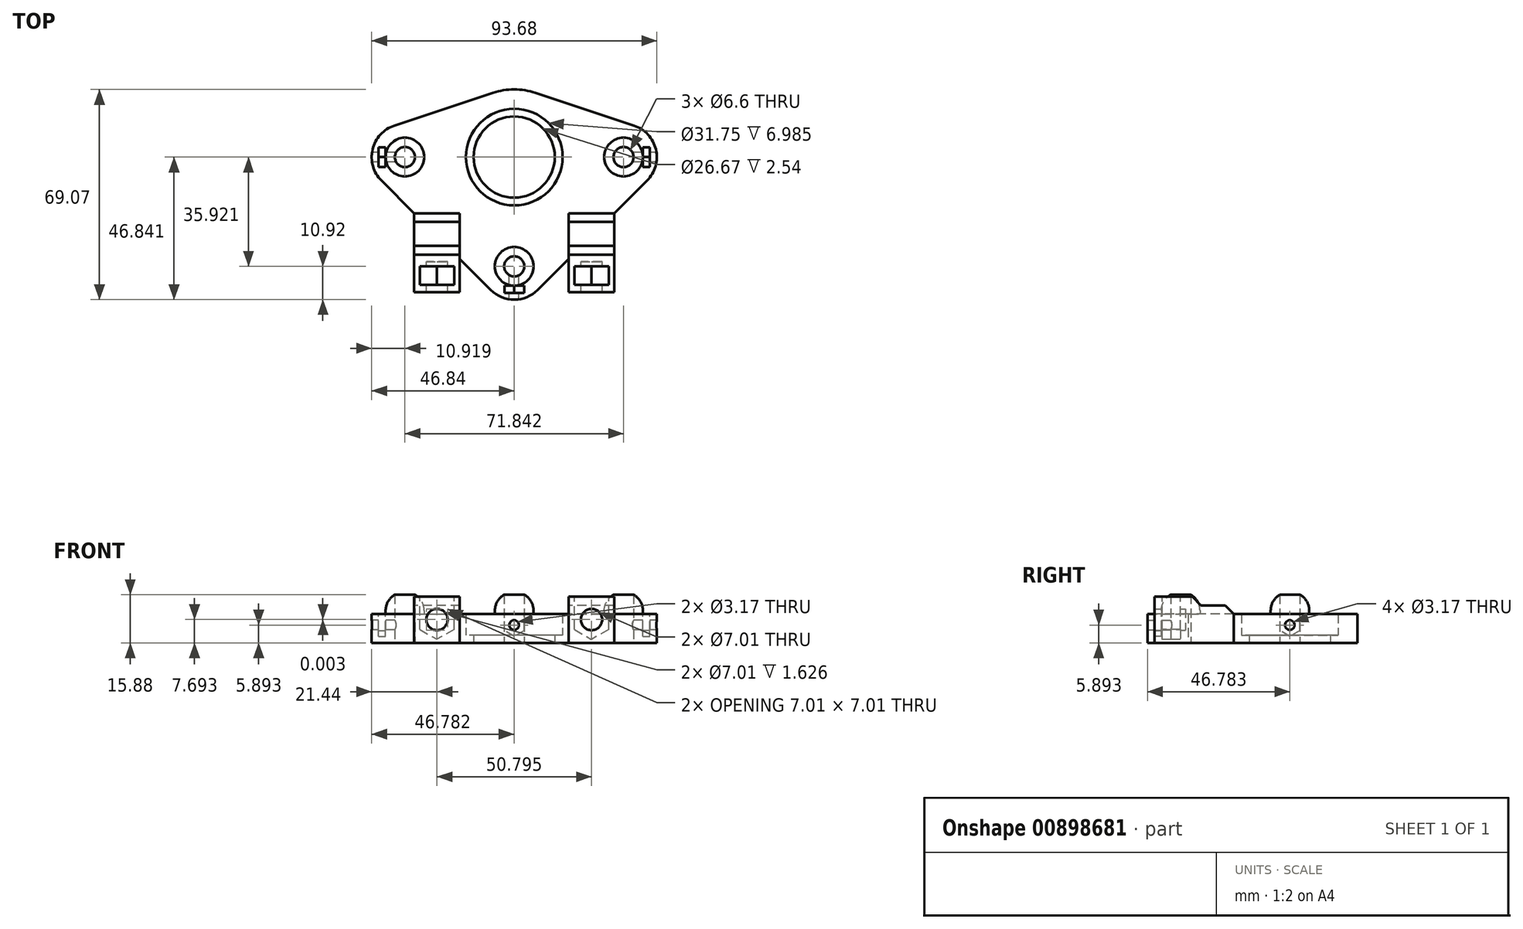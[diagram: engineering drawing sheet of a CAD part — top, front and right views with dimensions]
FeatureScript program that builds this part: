
annotation { "Feature Type Name" : "Feature", "Feature Type Description" : "" }
export const myFeature = defineFeature(function(context is Context, id is Id, definition is map)
    precondition{}
    {
        {
            var Q0;
            Q0=qCreatedBy(makeId("Top.planeOp"),FACE);
            var sketch = newSketch(context, id + "F0", { "sketchPlane" : qUnion([Q0])});
            skCircle(sketch, "E0", {"center": v(0, 35.92) * mm, "radius": 15.88 * mm});
            skArc(sketch, "E1.0", {"start": v(7, 57.02) * mm, "mid": v(0, 58.15) * mm, "end": v(-7, 57.02) * mm});
            skLineSegment(sketch, "E2", {"start": v(-39.36, 46.29) * mm, "end": v(-7, 57.02) * mm});
            skLineSegment(sketch, "E3", {"start": v(7, 57.02) * mm, "end": v(39.36, 46.29) * mm});
            skCircle(sketch, "E4.0", {"center": v(0, 35.92) * mm, "radius": 13.33 * mm});
            skLineSegment(sketch, "E5", {"start": v(0, 35.92) * mm, "end": v(0, 51.8) * mm, "construction": true});
            skLineSegment(sketch, "E6", {"start": v(-35.92, 35.92) * mm, "end": v(35.92, 35.92) * mm, "construction": true});
            skCircle(sketch, "E7", {"center": v(0, 0) * mm, "radius": 3.3 * mm});
            skCircle(sketch, "E8", {"center": v(35.92, 35.92) * mm, "radius": 3.3 * mm});
            skCircle(sketch, "E9", {"center": v(-35.92, 35.92) * mm, "radius": 3.3 * mm});
            skArc(sketch, "E10.0", {"start": v(-39.36, 46.29) * mm, "mid": v(-46.55, 38.44) * mm, "end": v(-43.64, 28.2) * mm});
            skArc(sketch, "E11.0", {"start": v(-7.72, -7.72) * mm, "mid": v(0, -10.92) * mm, "end": v(7.72, -7.72) * mm});
            skArc(sketch, "E12.0", {"start": v(43.64, 28.2) * mm, "mid": v(46.55, 38.44) * mm, "end": v(39.36, 46.29) * mm});
            skLineSegment(sketch, "E13", {"start": v(-43.64, 28.2) * mm, "end": v(-32.9, 17.46) * mm});
            skLineSegment(sketch, "E14", {"start": v(7.72, -7.72) * mm, "end": v(17.9, 2.45) * mm});
            skLineSegment(sketch, "E15", {"start": v(25.4, 9.95) * mm, "end": v(25.4, -8.53) * mm, "construction": true});
            skLineSegment(sketch, "E16", {"start": v(-25.4, 9.95) * mm, "end": v(-25.4, -8.53) * mm, "construction": true});
            skLineSegment(sketch, "E17", {"start": v(-32.9, 17.46) * mm, "end": v(-32.9, -8.53) * mm});
            skLineSegment(sketch, "E18", {"start": v(-32.9, -8.53) * mm, "end": v(-17.9, -8.53) * mm});
            skLineSegment(sketch, "E19", {"start": v(-17.9, -8.53) * mm, "end": v(-17.9, 2.45) * mm});
            skLineSegment(sketch, "E20", {"start": v(17.9, 2.45) * mm, "end": v(17.9, -8.53) * mm});
            skLineSegment(sketch, "E21", {"start": v(17.9, -8.53) * mm, "end": v(32.9, -8.53) * mm});
            skLineSegment(sketch, "E22", {"start": v(32.9, -8.53) * mm, "end": v(32.9, 17.46) * mm});
            skLineSegment(sketch, "E23.trimOffspring", {"start": v(-17.9, 2.45) * mm, "end": v(-7.72, -7.72) * mm});
            skLineSegment(sketch, "E24.trimOffspring", {"start": v(32.9, 17.46) * mm, "end": v(43.64, 28.2) * mm});
            skLineSegment(sketch, "E25", {"start": v(-32.9, 17.46) * mm, "end": v(-17.9, 2.45) * mm, "construction": true});
            skLineSegment(sketch, "E26", {"start": v(17.9, 2.45) * mm, "end": v(32.9, 17.46) * mm, "construction": true});
            skSolve(sketch);
        }
        {
            var Q0;
            Q0=makeQuery(id+"F0.imprint","IMPRINT",FACE,{"disambiguationData":[TD([[makeQuery(id+"F0.imprint","IMPRINT",EDGE,{"derivedFrom":sQuery(id+"F0.wireOp",EDGE,"E0")}),-1.0]])]});
            extrude(context, id + "F1", {"entities" : qUnion([Q0]), "depth" : 9.52 * mm, "offsetDistance" : 25.4 * mm});
        }
        {
            var Q0;
            Q0=makeQuery(id+"F0.imprint","IMPRINT",FACE,{"disambiguationData":[TD([[makeQuery(id+"F0.imprint","IMPRINT",EDGE,{"derivedFrom":sQuery(id+"F0.wireOp",EDGE,"E0")}),1.0]])]});
            var Q1;
            Q1=makeQuery(id+"F1.opExtrude","CAP_FACE",FACE,{"disambiguationData":[OSD([sQuery(id+"F0.wireOp",EDGE,"EjYE8rPL-0voM-13ep-dpKR-Yhmu4oC0fMjX"),sQuery(id+"F0.wireOp",EDGE,"BDsdlpYl-4XZS-kb72-SQzJ-jy24um5DGsSm"),sQuery(id+"F0.wireOp",EDGE,"zDj9rnkT-zBYQ-YRrf-FuGE-prHvdQQL9E0l"),sQuery(id+"F0.wireOp",EDGE,"E0"),sQuery(id+"F0.wireOp",EDGE,"be656b23-60e4-4951-9072-4bb9fd2c1fe0.0"),sQuery(id+"F0.wireOp",EDGE,"E1.0"),sQuery(id+"F0.wireOp",EDGE,"4a9f2f50-e787-4006-96f4-ab8e54a99077.0"),sQuery(id+"F0.wireOp",EDGE,"02fbeba7-076e-4ed0-9f02-67362b93dccf.0"),sQuery(id+"F0.wireOp",EDGE,"E2"),sQuery(id+"F0.wireOp",EDGE,"E3"),sQuery(id+"F0.wireOp",EDGE,"O9yRHGw0-B6N5-WUBC-CqYZ-9fVMz9zkHXct"),sQuery(id+"F0.wireOp",EDGE,"bXI39tXD-kIKO-QA8d-uo1d-AjNWw4kzWSzn"),sQuery(id+"F0.wireOp",EDGE,"yvXXFvSa-JQHm-aZvy-wO3q-0ffgoC5Wr51Q"),sQuery(id+"F0.wireOp",EDGE,"keBa6mA6-Ns36-as4S-D7yK-ubB9MYcM4YDE"),sQuery(id+"F0.wireOp",EDGE,"8eHimBAp-EooJ-JMgW-8GNK-FZK91k5yhUmU"),sQuery(id+"F0.wireOp",EDGE,"36RZBXD3-6qK0-qw5N-QxHJ-8RBiURi620yN"),sQuery(id+"F0.wireOp",EDGE,"1b80de2d-6fcf-4166-8bd7-bc7520118ab3.trimOffspring"),sQuery(id+"F0.wireOp",EDGE,"c2b8b45b-57a7-46a8-b7ff-993cbbd2993e.trimOffspring"),sQuery(id+"F0.wireOp",EDGE,"9e57da74-859c-4f91-937b-fdcaf8afdda5.filletArc"),sQuery(id+"F0.wireOp",EDGE,"30e6a12d-ff62-4460-809b-2951cf116d4f.filletArc"),sQuery(id+"F0.wireOp",EDGE,"3d167f00-72a4-4ff5-8a6d-0d591a0e7773.filletArc"),sQuery(id+"F0.wireOp",EDGE,"oY1VHBi5-08zZ-AYfj-pQcV-54PoHM0Vimur"),sQuery(id+"F0.wireOp",EDGE,"o9Ub0ZbI-FWSb-Ar0A-mzkB-0TMMgAmCBTNA"),sQuery(id+"F0.wireOp",EDGE,"02ed80ea-b338-46f1-988c-5186e078d909.trimOffspring"),sQuery(id+"F0.wireOp",EDGE,"5048e359-dd0b-4d89-8e95-103b38747b91.filletArc"),sQuery(id+"F0.wireOp",EDGE,"F9NU9Cbi-ggXa-7yM7-VtZo-IDbmedrVVywU"),sQuery(id+"F0.wireOp",EDGE,"RxFEJMYw-qQQS-0Qhc-ig3X-IfwXJgG6lVj4"),sQuery(id+"F0.wireOp",EDGE,"25558c64-657d-4b99-b26e-c29775e7ec7f.filletArc"),sQuery(id+"F0.wireOp",EDGE,"0ec6c237-3fc5-43e5-bd65-df81ba4ec1d8.filletArc"),sQuery(id+"F0.wireOp",EDGE,"df5fecd0-7309-4179-a44a-8c306f083116.filletArc"),sQuery(id+"F0.wireOp",EDGE,"e0a676b0-1f90-490a-bc8b-b1ab685ed8d2.filletArc")])],"isStart":false});
            extrude(context, id + "F2", {"entities" : qUnion([Q0]), "operationType" : NewBodyOperationType.ADD, "depth" : 2.54 * mm, "endBoundEntityFace" : qUnion([Q1]), "offsetDistance" : 6.35 * mm});
        }
        {
            var Q0;
            Q0=makeQuery(id+"F1.opExtrude","CAP_FACE",FACE,{"disambiguationData":[OSD([sQuery(id+"F0.wireOp",EDGE,"EjYE8rPL-0voM-13ep-dpKR-Yhmu4oC0fMjX"),sQuery(id+"F0.wireOp",EDGE,"BDsdlpYl-4XZS-kb72-SQzJ-jy24um5DGsSm"),sQuery(id+"F0.wireOp",EDGE,"zDj9rnkT-zBYQ-YRrf-FuGE-prHvdQQL9E0l"),sQuery(id+"F0.wireOp",EDGE,"E0"),sQuery(id+"F0.wireOp",EDGE,"be656b23-60e4-4951-9072-4bb9fd2c1fe0.0"),sQuery(id+"F0.wireOp",EDGE,"E1.0"),sQuery(id+"F0.wireOp",EDGE,"4a9f2f50-e787-4006-96f4-ab8e54a99077.0"),sQuery(id+"F0.wireOp",EDGE,"02fbeba7-076e-4ed0-9f02-67362b93dccf.0"),sQuery(id+"F0.wireOp",EDGE,"E2"),sQuery(id+"F0.wireOp",EDGE,"E3"),sQuery(id+"F0.wireOp",EDGE,"O9yRHGw0-B6N5-WUBC-CqYZ-9fVMz9zkHXct"),sQuery(id+"F0.wireOp",EDGE,"bXI39tXD-kIKO-QA8d-uo1d-AjNWw4kzWSzn"),sQuery(id+"F0.wireOp",EDGE,"yvXXFvSa-JQHm-aZvy-wO3q-0ffgoC5Wr51Q"),sQuery(id+"F0.wireOp",EDGE,"keBa6mA6-Ns36-as4S-D7yK-ubB9MYcM4YDE"),sQuery(id+"F0.wireOp",EDGE,"8eHimBAp-EooJ-JMgW-8GNK-FZK91k5yhUmU"),sQuery(id+"F0.wireOp",EDGE,"36RZBXD3-6qK0-qw5N-QxHJ-8RBiURi620yN"),sQuery(id+"F0.wireOp",EDGE,"1b80de2d-6fcf-4166-8bd7-bc7520118ab3.trimOffspring"),sQuery(id+"F0.wireOp",EDGE,"c2b8b45b-57a7-46a8-b7ff-993cbbd2993e.trimOffspring"),sQuery(id+"F0.wireOp",EDGE,"9e57da74-859c-4f91-937b-fdcaf8afdda5.filletArc"),sQuery(id+"F0.wireOp",EDGE,"30e6a12d-ff62-4460-809b-2951cf116d4f.filletArc"),sQuery(id+"F0.wireOp",EDGE,"3d167f00-72a4-4ff5-8a6d-0d591a0e7773.filletArc"),sQuery(id+"F0.wireOp",EDGE,"oY1VHBi5-08zZ-AYfj-pQcV-54PoHM0Vimur"),sQuery(id+"F0.wireOp",EDGE,"o9Ub0ZbI-FWSb-Ar0A-mzkB-0TMMgAmCBTNA"),sQuery(id+"F0.wireOp",EDGE,"02ed80ea-b338-46f1-988c-5186e078d909.trimOffspring"),sQuery(id+"F0.wireOp",EDGE,"3LgmcLzA-5pnU-fFz7-q1u9-bpeBtAsCO3An"),sQuery(id+"F0.wireOp",EDGE,"4eo9xTR6-c1Fu-en91-zOid-S4E7wj55DmDX"),sQuery(id+"F0.wireOp",EDGE,"5048e359-dd0b-4d89-8e95-103b38747b91.filletArc"),sQuery(id+"F0.wireOp",EDGE,"0de4be46-af92-408f-a28e-b5eb566cc358.filletArc"),sQuery(id+"F0.wireOp",EDGE,"cd97e584-8722-4711-bad1-4d169eb79cda.filletArc"),sQuery(id+"F0.wireOp",EDGE,"a80f9f6f-3806-41d0-9fd0-596e0330244b.filletArc"),sQuery(id+"F0.wireOp",EDGE,"743a1c7c-530f-41f0-bede-06812bb20fe3.filletArc")])],"isStart":false});
            var sketch = newSketch(context, id + "F3", { "sketchPlane" : qUnion([Q0])});
            skCircle(sketch, "E27", {"center": v(-35.92, 35.92) * mm, "radius": 6.35 * mm});
            skCircle(sketch, "E28", {"center": v(35.92, 35.92) * mm, "radius": 6.35 * mm});
            skCircle(sketch, "E29", {"center": v(0, 0) * mm, "radius": 6.35 * mm});
            skCircle(sketch, "E30.0", {"center": v(0, 35.92) * mm, "radius": 15.88 * mm});
            skCircle(sketch, "E31.0", {"center": v(0, 35.92) * mm, "radius": 19.05 * mm});
            skSolve(sketch);
        }
        {
            var Q0;
            Q0=makeQuery(id+"F1.opExtrude","CAP_FACE",FACE,{"disambiguationData":[OSD([sQuery(id+"F0.wireOp",EDGE,"EjYE8rPL-0voM-13ep-dpKR-Yhmu4oC0fMjX"),sQuery(id+"F0.wireOp",EDGE,"BDsdlpYl-4XZS-kb72-SQzJ-jy24um5DGsSm"),sQuery(id+"F0.wireOp",EDGE,"zDj9rnkT-zBYQ-YRrf-FuGE-prHvdQQL9E0l"),sQuery(id+"F0.wireOp",EDGE,"E0"),sQuery(id+"F0.wireOp",EDGE,"be656b23-60e4-4951-9072-4bb9fd2c1fe0.0"),sQuery(id+"F0.wireOp",EDGE,"E1.0"),sQuery(id+"F0.wireOp",EDGE,"4a9f2f50-e787-4006-96f4-ab8e54a99077.0"),sQuery(id+"F0.wireOp",EDGE,"02fbeba7-076e-4ed0-9f02-67362b93dccf.0"),sQuery(id+"F0.wireOp",EDGE,"E2"),sQuery(id+"F0.wireOp",EDGE,"E3"),sQuery(id+"F0.wireOp",EDGE,"O9yRHGw0-B6N5-WUBC-CqYZ-9fVMz9zkHXct"),sQuery(id+"F0.wireOp",EDGE,"bXI39tXD-kIKO-QA8d-uo1d-AjNWw4kzWSzn"),sQuery(id+"F0.wireOp",EDGE,"yvXXFvSa-JQHm-aZvy-wO3q-0ffgoC5Wr51Q"),sQuery(id+"F0.wireOp",EDGE,"keBa6mA6-Ns36-as4S-D7yK-ubB9MYcM4YDE"),sQuery(id+"F0.wireOp",EDGE,"8eHimBAp-EooJ-JMgW-8GNK-FZK91k5yhUmU"),sQuery(id+"F0.wireOp",EDGE,"36RZBXD3-6qK0-qw5N-QxHJ-8RBiURi620yN"),sQuery(id+"F0.wireOp",EDGE,"1b80de2d-6fcf-4166-8bd7-bc7520118ab3.trimOffspring"),sQuery(id+"F0.wireOp",EDGE,"c2b8b45b-57a7-46a8-b7ff-993cbbd2993e.trimOffspring"),sQuery(id+"F0.wireOp",EDGE,"9e57da74-859c-4f91-937b-fdcaf8afdda5.filletArc"),sQuery(id+"F0.wireOp",EDGE,"2f08ad09-a47d-42bd-8f0e-b7f58f6490e4.filletArc"),sQuery(id+"F0.wireOp",EDGE,"30e6a12d-ff62-4460-809b-2951cf116d4f.filletArc"),sQuery(id+"F0.wireOp",EDGE,"3d167f00-72a4-4ff5-8a6d-0d591a0e7773.filletArc"),sQuery(id+"F0.wireOp",EDGE,"oY1VHBi5-08zZ-AYfj-pQcV-54PoHM0Vimur"),sQuery(id+"F0.wireOp",EDGE,"o9Ub0ZbI-FWSb-Ar0A-mzkB-0TMMgAmCBTNA"),sQuery(id+"F0.wireOp",EDGE,"02ed80ea-b338-46f1-988c-5186e078d909.trimOffspring"),sQuery(id+"F0.wireOp",EDGE,"bfc3d6b4-ed7b-404a-8939-94d15189dd00.filletArc"),sQuery(id+"F0.wireOp",EDGE,"d06de643-c4a7-4e1d-b592-4d839de3a7a0.filletArc")])],"isStart":false});
            var sketch = newSketch(context, id + "F4", { "sketchPlane" : qUnion([Q0])});
            skPoint(sketch, "E32.center", {"position": v(0, 35.92) * mm});
            skCircle(sketch, "E33", {"center": v(-35.92, 35.92) * mm, "radius": 6.35 * mm});
            skCircle(sketch, "E34", {"center": v(35.92, 35.92) * mm, "radius": 6.35 * mm});
            skCircle(sketch, "E35", {"center": v(0, 0) * mm, "radius": 6.35 * mm});
            skLineSegment(sketch, "E36", {"start": v(-42.27, 39.15) * mm, "end": v(-42.27, 32.7) * mm});
            skLineSegment(sketch, "E37", {"start": v(-42.27, 32.7) * mm, "end": v(-44.6, 32.7) * mm});
            skLineSegment(sketch, "E38", {"start": v(-44.6, 32.7) * mm, "end": v(-44.6, 39.15) * mm});
            skLineSegment(sketch, "E39", {"start": v(-44.6, 39.15) * mm, "end": v(-42.27, 39.15) * mm});
            skLineSegment(sketch, "E40", {"start": v(-35.92, 35.92) * mm, "end": v(-42.27, 35.92) * mm, "construction": true});
            skLineSegment(sketch, "E41", {"start": v(42.27, 32.7) * mm, "end": v(42.27, 39.15) * mm});
            skLineSegment(sketch, "E42", {"start": v(42.27, 39.15) * mm, "end": v(44.6, 39.15) * mm});
            skLineSegment(sketch, "E43", {"start": v(44.6, 39.15) * mm, "end": v(44.6, 32.7) * mm});
            skLineSegment(sketch, "E44", {"start": v(44.6, 32.7) * mm, "end": v(42.27, 32.7) * mm});
            skLineSegment(sketch, "E45", {"start": v(35.92, 35.92) * mm, "end": v(42.27, 35.92) * mm, "construction": true});
            skLineSegment(sketch, "E46", {"start": v(3.23, -8.69) * mm, "end": v(-3.23, -8.69) * mm});
            skLineSegment(sketch, "E47", {"start": v(-3.23, -8.69) * mm, "end": v(-3.23, -6.35) * mm});
            skLineSegment(sketch, "E48", {"start": v(-3.23, -6.35) * mm, "end": v(3.23, -6.35) * mm});
            skLineSegment(sketch, "E49", {"start": v(3.23, -6.35) * mm, "end": v(3.23, -8.69) * mm});
            skLineSegment(sketch, "E50", {"start": v(0, -8.69) * mm, "end": v(0, 0) * mm, "construction": true});
            skSolve(sketch);
        }
        {
            var Q0;
            Q0=makeQuery(id+"F4.imprint","IMPRINT",FACE,{"disambiguationData":[TD([[makeQuery(id+"F4.imprint","IMPRINT",EDGE,{"derivedFrom":sQuery(id+"F4.wireOp",EDGE,"E32.2.0")}),-1.0]])]});
            var Q1;
            {var subQ3=sQuery(id+"F4.wireOp",EDGE,"d1FFw4VD-CotE-ErUC-aBlM-ySrozfUtPZIG");Q1=makeQuery(id+"F4.imprint","IMPRINT",FACE,{"disambiguationData":[TD([[makeQuery(id+"F4.imprint","IMPRINT",EDGE,{"derivedFrom":subQ3}),-1.0]])]});}
            var Q2;
            Q2=makeQuery(id+"F4.imprint","IMPRINT",FACE,{"disambiguationData":[TD([[makeQuery(id+"F4.imprint","IMPRINT",EDGE,{"derivedFrom":sQuery(id+"F4.wireOp",EDGE,"E32.1.0")}),-1.0]])]});
            var Q3;
            {var subQ0=sQuery(id+"F4.wireOp",EDGE,"E37");Q3=makeQuery(id+"F4.imprint","IMPRINT",FACE,{"disambiguationData":[TD([[makeQuery(id+"F4.imprint","IMPRINT",EDGE,{"derivedFrom":subQ0}),-1.0]])]});}
            var Q4;
            {var subQ0=sQuery(id+"F4.wireOp",EDGE,"E42");Q4=makeQuery(id+"F4.imprint","IMPRINT",FACE,{"disambiguationData":[TD([[makeQuery(id+"F4.imprint","IMPRINT",EDGE,{"derivedFrom":subQ0}),-1.0]])]});}
            var Q5;
            Q5=makeQuery(id+"F4.imprint","IMPRINT",FACE,{"disambiguationData":[TD([[makeQuery(id+"F4.imprint","IMPRINT",EDGE,{"derivedFrom":sQuery(id+"F4.wireOp",EDGE,"E46")}),-1.0]])]});
            extrude(context, id + "F5", {"entities" : qUnion([Q0, Q1, Q2, Q3, Q4, Q5]), "operationType" : NewBodyOperationType.REMOVE, "oppositeDirection" : true, "depth" : 8.64 * mm, "offsetDistance" : 25.4 * mm});
        }
        {
            var Q0;
            Q0=makeQuery(id+"F5.boolean.opBoolean","COPY",EDGE,{"derivedFrom":makeQuery(id+"F5.opExtrude","CAP_EDGE",EDGE,{"disambiguationData":[OSD([sQuery(id+"F4.wireOp",EDGE,"E32.1.1")])],"isStart":false})});
            var Q1;
            Q1=makeQuery(id+"F5.boolean.opBoolean","COPY",EDGE,{"derivedFrom":makeQuery(id+"F5.opExtrude","CAP_EDGE",EDGE,{"disambiguationData":[OSD([sQuery(id+"F4.wireOp",EDGE,"E32.1.3")])],"isStart":false})});
            var Q2;
            Q2=makeQuery(id+"F5.boolean.opBoolean","COPY",EDGE,{"derivedFrom":makeQuery(id+"F5.opExtrude","CAP_EDGE",EDGE,{"disambiguationData":[OSD([sQuery(id+"F4.wireOp",EDGE,"d1FFw4VD-CotE-ErUC-aBlM-ySrozfUtPZIG")])],"isStart":false})});
            var Q3;
            Q3=makeQuery(id+"F5.boolean.opBoolean","COPY",EDGE,{"derivedFrom":makeQuery(id+"F5.opExtrude","CAP_EDGE",EDGE,{"disambiguationData":[OSD([sQuery(id+"F4.wireOp",EDGE,"UtWCcdUI-wfrM-d3JI-pGr6-eE53RfRw4Zsa")])],"isStart":false})});
            var Q4;
            Q4=makeQuery(id+"F5.boolean.opBoolean","COPY",EDGE,{"derivedFrom":makeQuery(id+"F5.opExtrude","CAP_EDGE",EDGE,{"disambiguationData":[OSD([sQuery(id+"F4.wireOp",EDGE,"E32.2.3")])],"isStart":false})});
            var Q5;
            Q5=makeQuery(id+"F5.boolean.opBoolean","COPY",EDGE,{"derivedFrom":makeQuery(id+"F5.opExtrude","CAP_EDGE",EDGE,{"disambiguationData":[OSD([sQuery(id+"F4.wireOp",EDGE,"E32.2.1")])],"isStart":false})});
            var Q6;
            Q6=makeQuery(id+"F5.boolean.opBoolean","COPY",EDGE,{"derivedFrom":makeQuery(id+"F5.opExtrude","CAP_EDGE",EDGE,{"disambiguationData":[OSD([sQuery(id+"F4.wireOp",EDGE,"E39")])],"isStart":false})});
            var Q7;
            Q7=makeQuery(id+"F5.boolean.opBoolean","COPY",EDGE,{"derivedFrom":makeQuery(id+"F5.opExtrude","CAP_EDGE",EDGE,{"disambiguationData":[OSD([sQuery(id+"F4.wireOp",EDGE,"E37")])],"isStart":false})});
            var Q8;
            Q8=makeQuery(id+"F5.boolean.opBoolean","COPY",EDGE,{"derivedFrom":makeQuery(id+"F5.opExtrude","CAP_EDGE",EDGE,{"disambiguationData":[OSD([sQuery(id+"F4.wireOp",EDGE,"E49")])],"isStart":false})});
            var Q9;
            Q9=makeQuery(id+"F5.boolean.opBoolean","COPY",EDGE,{"derivedFrom":makeQuery(id+"F5.opExtrude","CAP_EDGE",EDGE,{"disambiguationData":[OSD([sQuery(id+"F4.wireOp",EDGE,"E47")])],"isStart":false})});
            var Q10;
            Q10=makeQuery(id+"F5.boolean.opBoolean","COPY",EDGE,{"derivedFrom":makeQuery(id+"F5.opExtrude","CAP_EDGE",EDGE,{"disambiguationData":[OSD([sQuery(id+"F4.wireOp",EDGE,"E42")])],"isStart":false})});
            var Q11;
            Q11=makeQuery(id+"F5.boolean.opBoolean","COPY",EDGE,{"derivedFrom":makeQuery(id+"F5.opExtrude","CAP_EDGE",EDGE,{"disambiguationData":[OSD([sQuery(id+"F4.wireOp",EDGE,"E44")])],"isStart":false})});
            chamfer(context, id + "F6", {"entities" : qUnion([Q0, Q1, Q2, Q3, Q4, Q5, Q6, Q7, Q8, Q9, Q10, Q11]), "chamferType" : ChamferType.OFFSET_ANGLE, "width" : 3.17 * mm, "oppositeDirection" : false, "angle" : 60 * degree, "tangentPropagation" : true});
        }
        {
            var Q0;
            Q0=makeQuery(id+"F3.imprint","IMPRINT",FACE,{"disambiguationData":[TD([[makeQuery(id+"F3.imprint","IMPRINT",EDGE,{"derivedFrom":sQuery(id+"F3.wireOp",EDGE,"E27")}),1.0]])]});
            var Q1;
            Q1=makeQuery(id+"F3.imprint","IMPRINT",FACE,{"disambiguationData":[TD([[makeQuery(id+"F3.imprint","IMPRINT",EDGE,{"derivedFrom":sQuery(id+"F3.wireOp",EDGE,"E29")}),1.0]])]});
            var Q2;
            Q2=makeQuery(id+"F3.imprint","IMPRINT",FACE,{"disambiguationData":[TD([[makeQuery(id+"F3.imprint","IMPRINT",EDGE,{"derivedFrom":sQuery(id+"F3.wireOp",EDGE,"E28")}),1.0]])]});
            extrude(context, id + "F7", {"entities" : qUnion([Q0, Q1, Q2]), "operationType" : NewBodyOperationType.ADD, "depth" : 6.35 * mm, "offsetDistance" : 25.4 * mm});
        }
        {
            var Q0;
            Q0=makeQuery(id+"F7.opExtrude","CAP_EDGE",EDGE,{"disambiguationData":[OSD([sQuery(id+"F3.wireOp",EDGE,"E27")])],"isStart":false});
            var Q1;
            Q1=makeQuery(id+"F7.opExtrude","CAP_EDGE",EDGE,{"disambiguationData":[OSD([sQuery(id+"F3.wireOp",EDGE,"E28")])],"isStart":false});
            var Q2;
            Q2=makeQuery(id+"F7.opExtrude","CAP_EDGE",EDGE,{"disambiguationData":[OSD([sQuery(id+"F3.wireOp",EDGE,"E29")])],"isStart":false});
            fillet(context, id + "F8", {"entities" : qUnion([Q0, Q1, Q2]), "radius" : 6.1 * mm, "tangentPropagation" : true, "allowEdgeOverflow" : false});
        }
        {
            var Q0;
            Q0=makeQuery(id+"F5.boolean.opBoolean","COPY",FACE,{"derivedFrom":makeQuery(id+"F5.opExtrude","SWEPT_FACE",FACE,{"disambiguationData":[OSD([sQuery(id+"F4.wireOp",EDGE,"E38")])]})});
            var sketch = newSketch(context, id + "F9", { "sketchPlane" : qUnion([Q0])});
            skLineSegment(sketch, "E51", {"start": v(39.03, 4.06) * mm, "end": v(35.86, 2.24) * mm});
            skLineSegment(sketch, "E52", {"start": v(35.86, 2.24) * mm, "end": v(32.7, 4.06) * mm});
            skLineSegment(sketch, "E53", {"start": v(32.7, 4.06) * mm, "end": v(32.7, 7.72) * mm});
            skLineSegment(sketch, "E54", {"start": v(39.03, 7.72) * mm, "end": v(39.03, 4.06) * mm});
            skLineSegment(sketch, "E55", {"start": v(39.03, 7.72) * mm, "end": v(35.86, 9.55) * mm});
            skLineSegment(sketch, "E56", {"start": v(35.86, 9.55) * mm, "end": v(32.7, 7.72) * mm});
            skLineSegment(sketch, "E57", {"start": v(35.86, 2.24) * mm, "end": v(35.86, 5.9) * mm, "construction": true});
            skLineSegment(sketch, "E58", {"start": v(35.86, 5.9) * mm, "end": v(32.7, 4.06) * mm, "construction": true});
            skLineSegment(sketch, "E59", {"start": v(35.86, 5.9) * mm, "end": v(39.03, 7.72) * mm, "construction": true});
            skLineSegment(sketch, "E60", {"start": v(35.86, 5.9) * mm, "end": v(35.86, 9.55) * mm, "construction": true});
            skCircle(sketch, "E61", {"center": v(35.86, 5.9) * mm, "radius": 1.59 * mm});
            skSolve(sketch);
        }
        {
            var Q0;
            Q0=makeQuery(id+"F5.boolean.opBoolean","COPY",FACE,{"derivedFrom":makeQuery(id+"F5.opExtrude","SWEPT_FACE",FACE,{"disambiguationData":[OSD([sQuery(id+"F4.wireOp",EDGE,"E46")])]})});
            var sketch = newSketch(context, id + "F10", { "sketchPlane" : qUnion([Q0])});
            skLineSegment(sketch, "E62", {"start": v(3.23, 4.06) * mm, "end": v(0.06, 2.24) * mm});
            skLineSegment(sketch, "E63", {"start": v(0.06, 2.24) * mm, "end": v(-3.1, 4.06) * mm});
            skLineSegment(sketch, "E64", {"start": v(-3.1, 4.06) * mm, "end": v(-3.1, 7.72) * mm});
            skLineSegment(sketch, "E65", {"start": v(3.23, 7.72) * mm, "end": v(3.23, 4.06) * mm});
            skLineSegment(sketch, "E66", {"start": v(3.23, 7.72) * mm, "end": v(0.06, 9.55) * mm});
            skLineSegment(sketch, "E67", {"start": v(0.06, 9.55) * mm, "end": v(-3.1, 7.72) * mm});
            skLineSegment(sketch, "E68", {"start": v(0.06, 2.24) * mm, "end": v(0.06, 5.9) * mm, "construction": true});
            skLineSegment(sketch, "E69", {"start": v(0.06, 5.9) * mm, "end": v(-3.1, 4.06) * mm, "construction": true});
            skLineSegment(sketch, "E70", {"start": v(0.06, 5.9) * mm, "end": v(3.23, 7.72) * mm, "construction": true});
            skLineSegment(sketch, "E71", {"start": v(0.06, 5.9) * mm, "end": v(0.06, 9.55) * mm, "construction": true});
            skCircle(sketch, "E72", {"center": v(0.06, 5.9) * mm, "radius": 1.59 * mm});
            skSolve(sketch);
        }
        {
            var Q0;
            Q0=makeQuery(id+"F5.boolean.opBoolean","COPY",FACE,{"derivedFrom":makeQuery(id+"F5.opExtrude","SWEPT_FACE",FACE,{"disambiguationData":[OSD([sQuery(id+"F4.wireOp",EDGE,"E43")])]})});
            var sketch = newSketch(context, id + "F11", { "sketchPlane" : qUnion([Q0])});
            skLineSegment(sketch, "E73", {"start": v(-32.7, 4.06) * mm, "end": v(-35.86, 2.24) * mm});
            skLineSegment(sketch, "E74", {"start": v(-35.86, 2.24) * mm, "end": v(-39.03, 4.06) * mm});
            skLineSegment(sketch, "E75", {"start": v(-39.03, 4.06) * mm, "end": v(-39.03, 7.72) * mm});
            skLineSegment(sketch, "E76", {"start": v(-32.7, 7.72) * mm, "end": v(-32.7, 4.06) * mm});
            skLineSegment(sketch, "E77", {"start": v(-32.7, 7.72) * mm, "end": v(-35.86, 9.55) * mm});
            skLineSegment(sketch, "E78", {"start": v(-35.86, 9.55) * mm, "end": v(-39.03, 7.72) * mm});
            skLineSegment(sketch, "E79", {"start": v(-35.86, 2.24) * mm, "end": v(-35.86, 5.9) * mm, "construction": true});
            skLineSegment(sketch, "E80", {"start": v(-35.86, 5.9) * mm, "end": v(-39.03, 4.06) * mm, "construction": true});
            skLineSegment(sketch, "E81", {"start": v(-35.86, 5.9) * mm, "end": v(-32.7, 7.72) * mm, "construction": true});
            skLineSegment(sketch, "E82", {"start": v(-35.86, 5.9) * mm, "end": v(-35.86, 9.55) * mm, "construction": true});
            skCircle(sketch, "E83", {"center": v(-35.86, 5.9) * mm, "radius": 1.59 * mm});
            skSolve(sketch);
        }
        {
            var Q0;
            Q0=makeQuery(id+"F11.imprint","IMPRINT",FACE,{"disambiguationData":[TD([[makeQuery(id+"F11.imprint","IMPRINT",EDGE,{"derivedFrom":sQuery(id+"F11.wireOp",EDGE,"E83")}),1.0]])]});
            var Q1;
            Q1=sQuery(id+"F11.wireOp",EDGE,"E83");
            extrude(context, id + "F12", {"entities" : qUnion([Q0]), "operationType" : NewBodyOperationType.REMOVE, "surfaceEntities" : qUnion([Q1]), "oppositeDirection" : true, "depth" : 12.7 * mm, "offsetDistance" : 25.4 * mm, "symmetric" : true});
        }
        {
            var Q0;
            Q0=makeQuery(id+"F9.imprint","IMPRINT",FACE,{"disambiguationData":[TD([[makeQuery(id+"F9.imprint","IMPRINT",EDGE,{"derivedFrom":sQuery(id+"F9.wireOp",EDGE,"E61")}),1.0]])]});
            extrude(context, id + "F13", {"entities" : qUnion([Q0]), "operationType" : NewBodyOperationType.REMOVE, "depth" : 12.7 * mm, "offsetDistance" : 25.4 * mm, "symmetric" : true});
        }
        {
            var Q0;
            Q0=makeQuery(id+"F10.imprint","IMPRINT",FACE,{"disambiguationData":[TD([[makeQuery(id+"F10.imprint","IMPRINT",EDGE,{"derivedFrom":sQuery(id+"F10.wireOp",EDGE,"E72")}),1.0]])]});
            extrude(context, id + "F14", {"entities" : qUnion([Q0]), "operationType" : NewBodyOperationType.REMOVE, "oppositeDirection" : true, "depth" : 16.76 * mm, "offsetDistance" : 25.4 * mm, "symmetric" : true});
        }
        {
            var Q0;
            Q0=makeQuery(id+"F1.opExtrude","CAP_FACE",FACE,{"disambiguationData":[OSD([sQuery(id+"F0.wireOp",EDGE,"E0"),sQuery(id+"F0.wireOp",EDGE,"E1.0"),sQuery(id+"F0.wireOp",EDGE,"E2"),sQuery(id+"F0.wireOp",EDGE,"E3"),sQuery(id+"F0.wireOp",EDGE,"E7"),sQuery(id+"F0.wireOp",EDGE,"E8"),sQuery(id+"F0.wireOp",EDGE,"E9"),sQuery(id+"F0.wireOp",EDGE,"E10.0"),sQuery(id+"F0.wireOp",EDGE,"E11.0"),sQuery(id+"F0.wireOp",EDGE,"E12.0"),sQuery(id+"F0.wireOp",EDGE,"E13"),sQuery(id+"F0.wireOp",EDGE,"E14"),sQuery(id+"F0.wireOp",EDGE,"E17"),sQuery(id+"F0.wireOp",EDGE,"E18"),sQuery(id+"F0.wireOp",EDGE,"E19"),sQuery(id+"F0.wireOp",EDGE,"E20"),sQuery(id+"F0.wireOp",EDGE,"E21"),sQuery(id+"F0.wireOp",EDGE,"E22"),sQuery(id+"F0.wireOp",EDGE,"E23.trimOffspring"),sQuery(id+"F0.wireOp",EDGE,"E24.trimOffspring")])],"isStart":false});
            var sketch = newSketch(context, id + "F15", { "sketchPlane" : qUnion([Q0])});
            skLineSegment(sketch, "E84", {"start": v(-17.9, -8.53) * mm, "end": v(-32.9, -8.53) * mm});
            skLineSegment(sketch, "E85", {"start": v(-32.9, -8.53) * mm, "end": v(-32.9, 17.46) * mm});
            skLineSegment(sketch, "E86", {"start": v(-32.9, 17.46) * mm, "end": v(-17.9, 17.46) * mm});
            skLineSegment(sketch, "E87", {"start": v(-17.9, 17.46) * mm, "end": v(-17.9, -8.53) * mm});
            skLineSegment(sketch, "E88", {"start": v(17.9, -8.53) * mm, "end": v(32.9, -8.53) * mm});
            skLineSegment(sketch, "E89", {"start": v(32.9, -8.53) * mm, "end": v(32.9, 17.46) * mm});
            skLineSegment(sketch, "E90", {"start": v(32.9, 17.46) * mm, "end": v(17.9, 17.46) * mm});
            skPoint(sketch, "E90.endSnap0", {"position": v(17.9, -3.04) * mm});
            skLineSegment(sketch, "E91", {"start": v(17.9, 17.46) * mm, "end": v(17.9, -8.53) * mm});
            skLineSegment(sketch, "E92", {"start": v(-32.9, 6.71) * mm, "end": v(-17.9, 6.71) * mm});
            skLineSegment(sketch, "E93", {"start": v(17.9, 6.71) * mm, "end": v(32.9, 6.71) * mm});
            skSolve(sketch);
        }
        {
            var Q0;
            {var subQ3=sQuery(id+"F15.wireOp",EDGE,"E88");Q0=makeQuery(id+"F15.imprint","IMPRINT",FACE,{"disambiguationData":[TD([[makeQuery(id+"F15.imprint","IMPRINT",EDGE,{"derivedFrom":subQ3}),1.0]])]});}
            var Q1;
            {var subQ3=sQuery(id+"F15.wireOp",EDGE,"E84");Q1=makeQuery(id+"F15.imprint","IMPRINT",FACE,{"disambiguationData":[TD([[makeQuery(id+"F15.imprint","IMPRINT",EDGE,{"derivedFrom":subQ3}),1.0]])]});}
            extrude(context, id + "F16", {"entities" : qUnion([Q0, Q1]), "operationType" : NewBodyOperationType.ADD, "depth" : 5.66 * mm, "offsetDistance" : 25.4 * mm});
        }
        {
            var Q0;
            {var subQ0=sQuery(id+"F15.wireOp",EDGE,"E86");Q0=makeQuery(id+"F15.imprint","IMPRINT",FACE,{"disambiguationData":[TD([[makeQuery(id+"F15.imprint","IMPRINT",EDGE,{"derivedFrom":subQ0}),-1.0]])]});}
            var Q1;
            {var subQ0=sQuery(id+"F15.wireOp",EDGE,"E90");Q1=makeQuery(id+"F15.imprint","IMPRINT",FACE,{"disambiguationData":[TD([[makeQuery(id+"F15.imprint","IMPRINT",EDGE,{"derivedFrom":subQ0}),1.0]])]});}
            extrude(context, id + "F17", {"entities" : qUnion([Q0, Q1]), "operationType" : NewBodyOperationType.ADD, "depth" : 2.84 * mm, "offsetDistance" : 25.4 * mm});
        }
        {
            var Q0;
            Q0=makeQuery(id+"F17.opExtrude","CAP_EDGE",EDGE,{"disambiguationData":[OSD([sQuery(id+"F15.wireOp",EDGE,"E86")])],"isStart":false});
            var Q1;
            Q1=makeQuery(id+"F17.opExtrude","CAP_EDGE",EDGE,{"disambiguationData":[OSD([sQuery(id+"F15.wireOp",EDGE,"E90")])],"isStart":false});
            var Q2;
            Q2=makeQuery(id+"F16.opExtrude","CAP_EDGE",EDGE,{"disambiguationData":[OSD([sQuery(id+"F15.wireOp",EDGE,"E92")])],"isStart":false});
            var Q3;
            Q3=makeQuery(id+"F16.opExtrude","CAP_EDGE",EDGE,{"disambiguationData":[OSD([sQuery(id+"F15.wireOp",EDGE,"E93")])],"isStart":false});
            chamfer(context, id + "F18", {"entities" : qUnion([Q0, Q1, Q2, Q3]), "width" : 2.84 * mm, "tangentPropagation" : true});
        }
        {
            var Q0;
            Q0=makeQuery(id+"F16.opExtrude","CAP_FACE",FACE,{"disambiguationData":[OSD([sQuery(id+"F15.wireOp",EDGE,"E84"),sQuery(id+"F15.wireOp",EDGE,"E85"),sQuery(id+"F15.wireOp",EDGE,"E87"),sQuery(id+"F15.wireOp",EDGE,"E92")])],"isStart":false});
            var sketch = newSketch(context, id + "F19", { "sketchPlane" : qUnion([Q0])});
            skLineSegment(sketch, "E94.bottom", {"start": v(-31.03, -0.05) * mm, "end": v(-19.77, -0.05) * mm});
            skLineSegment(sketch, "E94.top", {"start": v(-31.03, -6.04) * mm, "end": v(-19.77, -6.04) * mm});
            skLineSegment(sketch, "E94.left", {"start": v(-31.03, -0.05) * mm, "end": v(-31.03, -6.04) * mm});
            skLineSegment(sketch, "E94.right", {"start": v(-19.77, -0.05) * mm, "end": v(-19.77, -6.04) * mm});
            skLineSegment(sketch, "E95.bottom", {"start": v(19.77, -0.05) * mm, "end": v(31.03, -0.05) * mm});
            skLineSegment(sketch, "E95.top", {"start": v(19.77, -6.04) * mm, "end": v(31.03, -6.04) * mm});
            skLineSegment(sketch, "E95.left", {"start": v(19.77, -0.05) * mm, "end": v(19.77, -6.04) * mm});
            skLineSegment(sketch, "E95.right", {"start": v(31.03, -0.05) * mm, "end": v(31.03, -6.04) * mm});
            skLineSegment(sketch, "E96", {"start": v(-32.9, -2.33) * mm, "end": v(-17.9, -2.33) * mm, "construction": true});
            skLineSegment(sketch, "E97", {"start": v(-25.4, -0.05) * mm, "end": v(-25.4, -8.53) * mm, "construction": true});
            skLineSegment(sketch, "E98", {"start": v(25.4, -0.05) * mm, "end": v(25.4, -6.04) * mm, "construction": true});
            skSolve(sketch);
        }
        {
            var Q0;
            Q0=makeQuery(id+"F19.imprint","IMPRINT",FACE,{"disambiguationData":[TD([[makeQuery(id+"F19.imprint","IMPRINT",EDGE,{"derivedFrom":sQuery(id+"F19.wireOp",EDGE,"E94.bottom")}),-1.0]])]});
            var Q1;
            Q1=makeQuery(id+"F19.imprint","IMPRINT",FACE,{"disambiguationData":[TD([[makeQuery(id+"F19.imprint","IMPRINT",EDGE,{"derivedFrom":sQuery(id+"F19.wireOp",EDGE,"E95.bottom")}),-1.0]])]});
            extrude(context, id + "F20", {"entities" : qUnion([Q0, Q1]), "operationType" : NewBodyOperationType.REMOVE, "oppositeDirection" : true, "depth" : 14 * mm, "offsetDistance" : 25.4 * mm});
        }
        {
            var Q0;
            Q0=makeQuery(id+"F20.boolean.opBoolean","COPY",EDGE,{"derivedFrom":makeQuery(id+"F20.opExtrude","CAP_EDGE",EDGE,{"disambiguationData":[OSD([sQuery(id+"F19.wireOp",EDGE,"E94.right")])],"isStart":false})});
            var Q1;
            Q1=makeQuery(id+"F20.boolean.opBoolean","COPY",EDGE,{"derivedFrom":makeQuery(id+"F20.opExtrude","CAP_EDGE",EDGE,{"disambiguationData":[OSD([sQuery(id+"F19.wireOp",EDGE,"E94.left")])],"isStart":false})});
            var Q2;
            Q2=makeQuery(id+"F20.boolean.opBoolean","COPY",EDGE,{"derivedFrom":makeQuery(id+"F20.opExtrude","CAP_EDGE",EDGE,{"disambiguationData":[OSD([sQuery(id+"F19.wireOp",EDGE,"E95.right")])],"isStart":false})});
            chamfer(context, id + "F21", {"entities" : qUnion([Q0, Q1, Q2]), "chamferType" : ChamferType.OFFSET_ANGLE, "width" : 3.25 * mm, "oppositeDirection" : false, "angle" : 60 * degree, "tangentPropagation" : true});
        }
        {
            var Q0;
            Q0=makeQuery(id+"F20.boolean.opBoolean","COPY",EDGE,{"derivedFrom":makeQuery(id+"F20.opExtrude","CAP_EDGE",EDGE,{"disambiguationData":[OSD([sQuery(id+"F19.wireOp",EDGE,"E95.left")])],"isStart":false})});
            chamfer(context, id + "F22", {"entities" : qUnion([Q0]), "chamferType" : ChamferType.OFFSET_ANGLE, "width" : 5.61 * mm, "oppositeDirection" : false, "angle" : 30 * degree, "tangentPropagation" : true});
        }
        {
            var Q0;
            Q0=makeQuery(id+"F20.boolean.opBoolean","COPY",FACE,{"derivedFrom":makeQuery(id+"F20.opExtrude","SWEPT_FACE",FACE,{"disambiguationData":[OSD([sQuery(id+"F19.wireOp",EDGE,"E94.top")])]})});
            var sketch = newSketch(context, id + "F23", { "sketchPlane" : qUnion([Q0])});
            skLineSegment(sketch, "E99", {"start": v(31.03, 4.44) * mm, "end": v(25.4, 1.2) * mm, "construction": true});
            skLineSegment(sketch, "E100", {"start": v(25.4, 1.2) * mm, "end": v(19.77, 4.44) * mm, "construction": true});
            skLineSegment(sketch, "E101", {"start": v(19.77, 4.44) * mm, "end": v(19.77, 10.94) * mm, "construction": true});
            skLineSegment(sketch, "E102", {"start": v(19.77, 10.94) * mm, "end": v(25.4, 14.19) * mm, "construction": true});
            skLineSegment(sketch, "E103", {"start": v(25.4, 14.19) * mm, "end": v(31.03, 10.94) * mm, "construction": true});
            skLineSegment(sketch, "E104", {"start": v(31.03, 10.94) * mm, "end": v(31.03, 4.44) * mm, "construction": true});
            skLineSegment(sketch, "E105", {"start": v(31.03, 4.44) * mm, "end": v(25.4, 7.7) * mm, "construction": true});
            skLineSegment(sketch, "E106", {"start": v(25.4, 7.7) * mm, "end": v(19.77, 10.94) * mm, "construction": true});
            skLineSegment(sketch, "E107", {"start": v(25.4, 1.2) * mm, "end": v(25.4, 7.7) * mm, "construction": true});
            skLineSegment(sketch, "E108", {"start": v(25.4, 7.7) * mm, "end": v(25.4, 14.19) * mm, "construction": true});
            skCircle(sketch, "E109", {"center": v(25.4, 7.7) * mm, "radius": 3.5 * mm});
            skSolve(sketch);
        }
        {
            var Q0;
            Q0=makeQuery(id+"F20.boolean.opBoolean","COPY",FACE,{"derivedFrom":makeQuery(id+"F20.opExtrude","SWEPT_FACE",FACE,{"disambiguationData":[OSD([sQuery(id+"F19.wireOp",EDGE,"E95.top")])]})});
            var sketch = newSketch(context, id + "F24", { "sketchPlane" : qUnion([Q0])});
            skLineSegment(sketch, "E110", {"start": v(-19.76, 4.44) * mm, "end": v(-25.4, 1.2) * mm, "construction": true});
            skLineSegment(sketch, "E111", {"start": v(-25.4, 1.2) * mm, "end": v(-31.03, 4.44) * mm, "construction": true});
            skLineSegment(sketch, "E112", {"start": v(-31.03, 4.44) * mm, "end": v(-31.03, 10.95) * mm, "construction": true});
            skLineSegment(sketch, "E113", {"start": v(-31.03, 10.95) * mm, "end": v(-25.4, 14.2) * mm, "construction": true});
            skLineSegment(sketch, "E114", {"start": v(-25.4, 14.2) * mm, "end": v(-19.76, 10.95) * mm, "construction": true});
            skLineSegment(sketch, "E115", {"start": v(-19.76, 10.95) * mm, "end": v(-19.76, 4.44) * mm, "construction": true});
            skLineSegment(sketch, "E116", {"start": v(-19.76, 4.44) * mm, "end": v(-25.4, 7.7) * mm, "construction": true});
            skLineSegment(sketch, "E117", {"start": v(-25.4, 7.7) * mm, "end": v(-31.03, 10.95) * mm, "construction": true});
            skLineSegment(sketch, "E118", {"start": v(-25.4, 1.2) * mm, "end": v(-25.4, 7.7) * mm, "construction": true});
            skLineSegment(sketch, "E119", {"start": v(-25.4, 7.7) * mm, "end": v(-25.4, 14.2) * mm, "construction": true});
            skCircle(sketch, "E120", {"center": v(-25.4, 7.7) * mm, "radius": 3.5 * mm});
            skSolve(sketch);
        }
        {
            var Q0;
            Q0=makeQuery(id+"F23.imprint","IMPRINT",FACE,{"disambiguationData":[TD([[makeQuery(id+"F23.imprint","IMPRINT",EDGE,{"derivedFrom":sQuery(id+"F23.wireOp",EDGE,"E109")}),1.0]])]});
            var Q1;
            Q1=makeQuery(id+"F24.imprint","IMPRINT",FACE,{"disambiguationData":[TD([[makeQuery(id+"F24.imprint","IMPRINT",EDGE,{"derivedFrom":sQuery(id+"F24.wireOp",EDGE,"E120")}),1.0]])]});
            extrude(context, id + "F25", {"entities" : qUnion([Q0, Q1]), "operationType" : NewBodyOperationType.REMOVE, "oppositeDirection" : true, "depth" : 15.24 * mm, "offsetDistance" : 25.4 * mm, "symmetric" : true});
        }
    });
